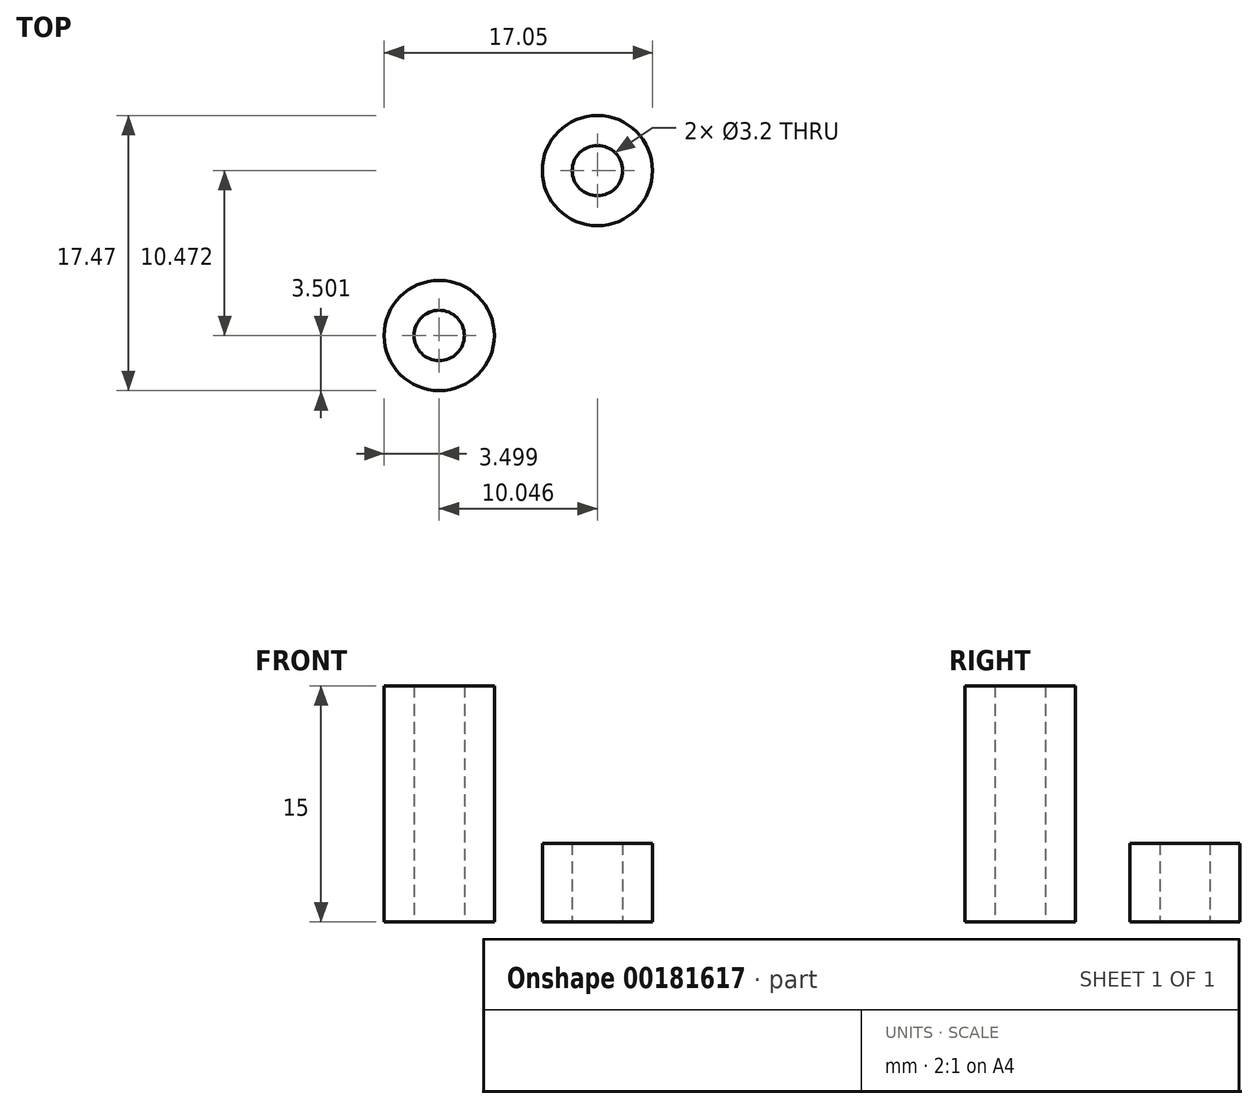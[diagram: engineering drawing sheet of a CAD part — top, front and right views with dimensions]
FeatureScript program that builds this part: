
annotation { "Feature Type Name" : "Feature", "Feature Type Description" : "" }
export const myFeature = defineFeature(function(context is Context, id is Id, definition is map)
    precondition{}
    {
        {
            var Q0;
            Q0=qCreatedBy(makeId("Top.planeOp"),FACE);
            var sketch = newSketch(context, id + "F0", { "sketchPlane" : qUnion([Q0])});
            skCircle(sketch, "E0", {"center": v(-37.94, 23.1) * mm, "radius": 1.6 * mm});
            skCircle(sketch, "E1", {"center": v(-37.94, 23.1) * mm, "radius": 3.5 * mm});
            skCircle(sketch, "E2", {"center": v(-48, 12.62) * mm, "radius": 1.6 * mm});
            skCircle(sketch, "E3", {"center": v(-48, 12.62) * mm, "radius": 3.5 * mm});
            skSolve(sketch);
        }
        {
            var Q0;
            Q0=makeQuery(id+"F0.imprint","IMPRINT",FACE,{"disambiguationData":[TD([[makeQuery(id+"F0.imprint","IMPRINT",EDGE,{"derivedFrom":sQuery(id+"F0.wireOp",EDGE,"E0")}),-1.0]])]});
            extrude(context, id + "F1", {"entities" : qUnion([Q0]), "depth" : 5 * mm});
        }
        {
            var Q0;
            Q0=makeQuery(id+"F0.imprint","IMPRINT",FACE,{"disambiguationData":[TD([[makeQuery(id+"F0.imprint","IMPRINT",EDGE,{"derivedFrom":sQuery(id+"F0.wireOp",EDGE,"E2")}),-1.0]])]});
            extrude(context, id + "F2", {"entities" : qUnion([Q0]), "depth" : 15 * mm});
        }
    });
